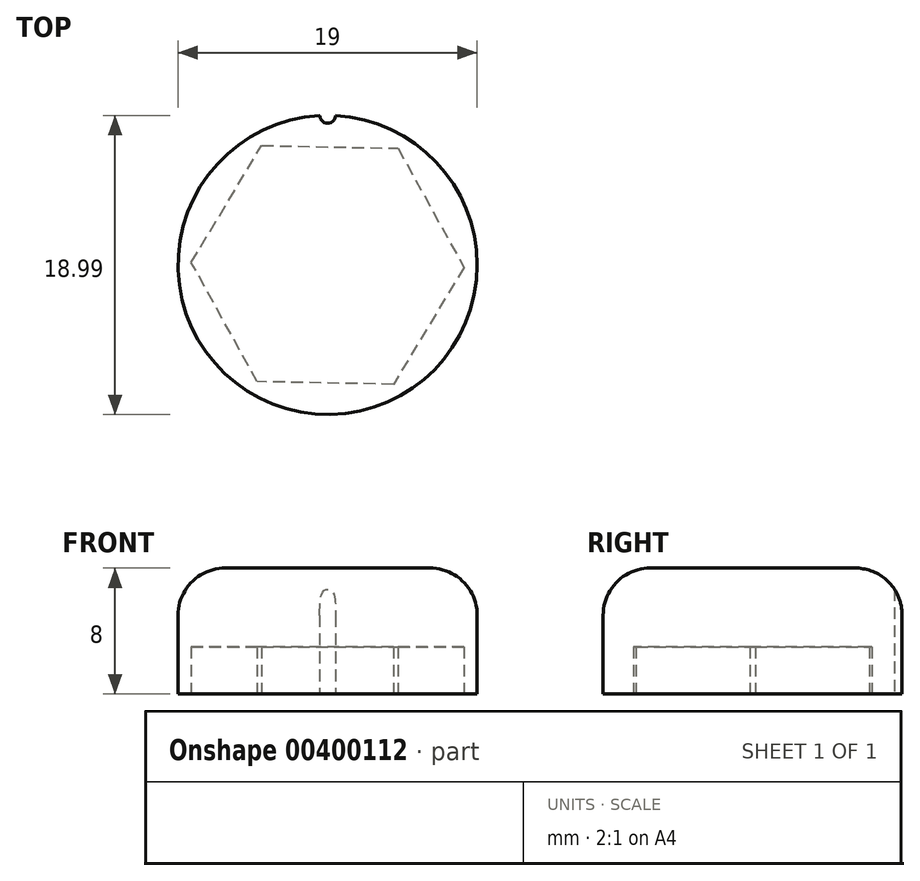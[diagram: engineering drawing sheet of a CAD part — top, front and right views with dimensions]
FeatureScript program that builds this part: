
annotation { "Feature Type Name" : "Feature", "Feature Type Description" : "" }
export const myFeature = defineFeature(function(context is Context, id is Id, definition is map)
    precondition{}
    {
        {
            var Q0;
            Q0=qCreatedBy(makeId("Top.planeOp"),FACE);
            var sketch = newSketch(context, id + "F0", { "sketchPlane" : qUnion([Q0])});
            skCircle(sketch, "E0.cCircle", {"center": v(0, 0) * mm, "radius": 7.5 * mm, "construction": true});
            skLineSegment(sketch, "E0.0", {"start": v(4.47, 7.42) * mm, "end": v(8.66, -0.17) * mm});
            skLineSegment(sketch, "E0.1", {"start": v(8.66, -0.17) * mm, "end": v(4.19, -7.58) * mm});
            skLineSegment(sketch, "E0.2", {"start": v(4.19, -7.58) * mm, "end": v(-4.47, -7.42) * mm});
            skLineSegment(sketch, "E0.3", {"start": v(-4.47, -7.42) * mm, "end": v(-8.66, 0.17) * mm});
            skLineSegment(sketch, "E0.4", {"start": v(-8.66, 0.17) * mm, "end": v(-4.19, 7.58) * mm});
            skLineSegment(sketch, "E0.5", {"start": v(-4.19, 7.58) * mm, "end": v(4.47, 7.42) * mm});
            skPoint(sketch, "E0.0.midPoint", {"position": v(6.57, 3.62) * mm});
            skCircle(sketch, "E1", {"center": v(0, 0) * mm, "radius": 9.5 * mm});
            skSolve(sketch);
        }
        {
            var Q0;
            Q0=makeQuery(id+"F0.imprint","IMPRINT",FACE,{"disambiguationData":[TD([[makeQuery(id+"F0.imprint","IMPRINT",EDGE,{"derivedFrom":sQuery(id+"F0.wireOp",EDGE,"E0.0")}),1.0]])]});
            extrude(context, id + "F1", {"entities" : qUnion([Q0]), "depth" : 3 * mm});
        }
        {
            var Q0;
            Q0=makeQuery(id+"F1.opExtrude","CAP_FACE",FACE,{"disambiguationData":[OSD([sQuery(id+"F0.wireOp",EDGE,"E0.0"),sQuery(id+"F0.wireOp",EDGE,"E0.1"),sQuery(id+"F0.wireOp",EDGE,"E0.2"),sQuery(id+"F0.wireOp",EDGE,"E0.3"),sQuery(id+"F0.wireOp",EDGE,"E0.4"),sQuery(id+"F0.wireOp",EDGE,"E0.5"),sQuery(id+"F0.wireOp",EDGE,"E1")])],"isStart":false});
            var sketch = newSketch(context, id + "F2", { "sketchPlane" : qUnion([Q0])});
            skCircle(sketch, "E2.0", {"center": v(0, 0) * mm, "radius": 9.5 * mm});
            skSolve(sketch);
        }
        {
            var Q0;
            Q0 = qSketchRegion(id + "F2", true);
            extrude(context, id + "F3", {"entities" : qUnion([Q0]), "operationType" : NewBodyOperationType.ADD, "depth" : 5 * mm});
        }
        {
            var Q0;
            Q0=makeQuery(id+"F3.opExtrude","CAP_EDGE",EDGE,{"disambiguationData":[OSD([sQuery(id+"F2.wireOp",EDGE,"E2.0")])],"isStart":false});
            fillet(context, id + "F4", {"entities" : qUnion([Q0]), "radius" : 3 * mm, "tangentPropagation" : true, "allowEdgeOverflow" : false});
        }
        {
            var Q0;
            Q0=makeQuery(id+"F1.opExtrude","CAP_FACE",FACE,{"disambiguationData":[OSD([sQuery(id+"F0.wireOp",EDGE,"E0.0"),sQuery(id+"F0.wireOp",EDGE,"E0.1"),sQuery(id+"F0.wireOp",EDGE,"E0.2"),sQuery(id+"F0.wireOp",EDGE,"E0.3"),sQuery(id+"F0.wireOp",EDGE,"E0.4"),sQuery(id+"F0.wireOp",EDGE,"E0.5"),sQuery(id+"F0.wireOp",EDGE,"E1")])],"isStart":true});
            var sketch = newSketch(context, id + "F5", { "sketchPlane" : qUnion([Q0])});
            skCircle(sketch, "E3", {"center": v(0, -9.5) * mm, "radius": 0.5 * mm});
            skSolve(sketch);
        }
        {
            var Q0;
            {var subQ0=sQuery(id+"F5.wireOp",EDGE,"E3");var subQ1=makeQuery(id+"F1.opExtrude","CAP_EDGE",EDGE,{"disambiguationData":[OSD([sQuery(id+"F0.wireOp",EDGE,"E1")])],"isStart":true});var subQ2=makeQuery(id+"F5.imprint","INTERSECT",VERTEX,{"disambiguationData":[OD(0.0)],"derivedFrom":[subQ1,subQ0]});Q0=makeQuery(id+"F5.imprint","IMPRINT",FACE,{"disambiguationData":[TD([[makeQuery(id+"F5.imprint","IMPRINT",EDGE,{"disambiguationData":[TD([[subQ2,1.0]])],"derivedFrom":subQ0}),1.0]])]});}
            extrude(context, id + "F6", {"entities" : qUnion([Q0]), "operationType" : NewBodyOperationType.REMOVE, "endBound" : BoundingType.THROUGH_ALL, "oppositeDirection" : true, "depth" : 25 * mm});
        }
    });
